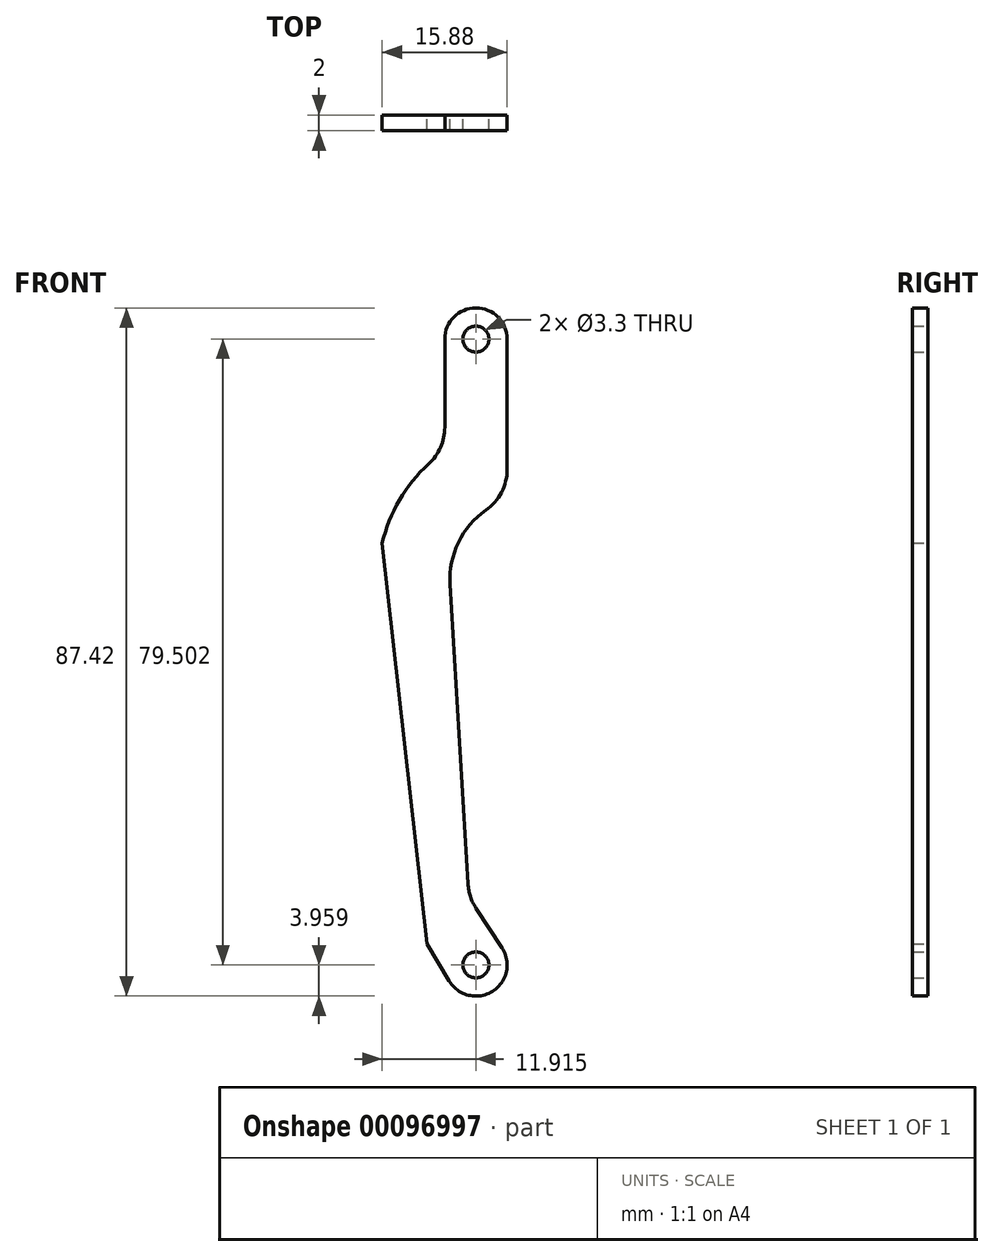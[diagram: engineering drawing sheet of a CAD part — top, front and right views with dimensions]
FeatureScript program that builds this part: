
annotation { "Feature Type Name" : "Feature", "Feature Type Description" : "" }
export const myFeature = defineFeature(function(context is Context, id is Id, definition is map)
    precondition{}
    {
        {
            var Q0;
            Q0=qCreatedBy(makeId("Front.planeOp"),FACE);
            var sketch = newSketch(context, id + "F0", { "sketchPlane" : qUnion([Q0])});
            skCircle(sketch, "E0", {"center": v(3.98, -39.75) * mm, "radius": 1.65 * mm});
            skCircle(sketch, "E1", {"center": v(3.98, 39.75) * mm, "radius": 1.65 * mm});
            skArc(sketch, "E2", {"start": v(7.94, 39.75) * mm, "mid": v(3.98, 43.71) * mm, "end": v(0.01, 39.75) * mm});
            skLineSegment(sketch, "E3", {"start": v(0.01, 39.75) * mm, "end": v(0.01, 28.56) * mm});
            skLineSegment(sketch, "E4", {"start": v(7.94, 39.75) * mm, "end": v(7.94, 23.22) * mm});
            skArc(sketch, "E5", {"start": v(5.23, 18.01) * mm, "mid": v(1.74, 13.91) * mm, "end": v(0.7, 8.63) * mm});
            skArc(sketch, "E6", {"start": v(-2.05, 23.88) * mm, "mid": v(-5.75, 19.3) * mm, "end": v(-7.94, 13.84) * mm});
            skArc(sketch, "E7", {"start": v(2.97, -29.46) * mm, "mid": v(3.28, -31.08) * mm, "end": v(4, -32.57) * mm});
            skArc(sketch, "E8", {"start": v(0.57, -41.79) * mm, "mid": v(6.08, -43.1) * mm, "end": v(7.29, -37.58) * mm});
            skLineSegment(sketch, "E9", {"start": v(4, -32.57) * mm, "end": v(7.29, -37.58) * mm});
            skLineSegment(sketch, "E10", {"start": v(0.7, 8.63) * mm, "end": v(2.97, -29.46) * mm});
            skArc(sketch, "E11", {"start": v(-2.05, 23.88) * mm, "mid": v(-0.52, 26) * mm, "end": v(0.01, 28.56) * mm});
            skArc(sketch, "E12", {"start": v(5.23, 18.01) * mm, "mid": v(7.22, 20.28) * mm, "end": v(7.94, 23.22) * mm});
            skLineSegment(sketch, "E13", {"start": v(-7.94, 13.84) * mm, "end": v(-2.22, -37.1) * mm});
            skLineSegment(sketch, "E14", {"start": v(-2.22, -37.1) * mm, "end": v(0.57, -41.79) * mm});
            skSolve(sketch);
        }
        {
            var Q0;
            Q0 = qSketchRegion(id + "F0", true);
            extrude(context, id + "F1", {"entities" : qUnion([Q0]), "depth" : 2 * mm});
        }
    });
